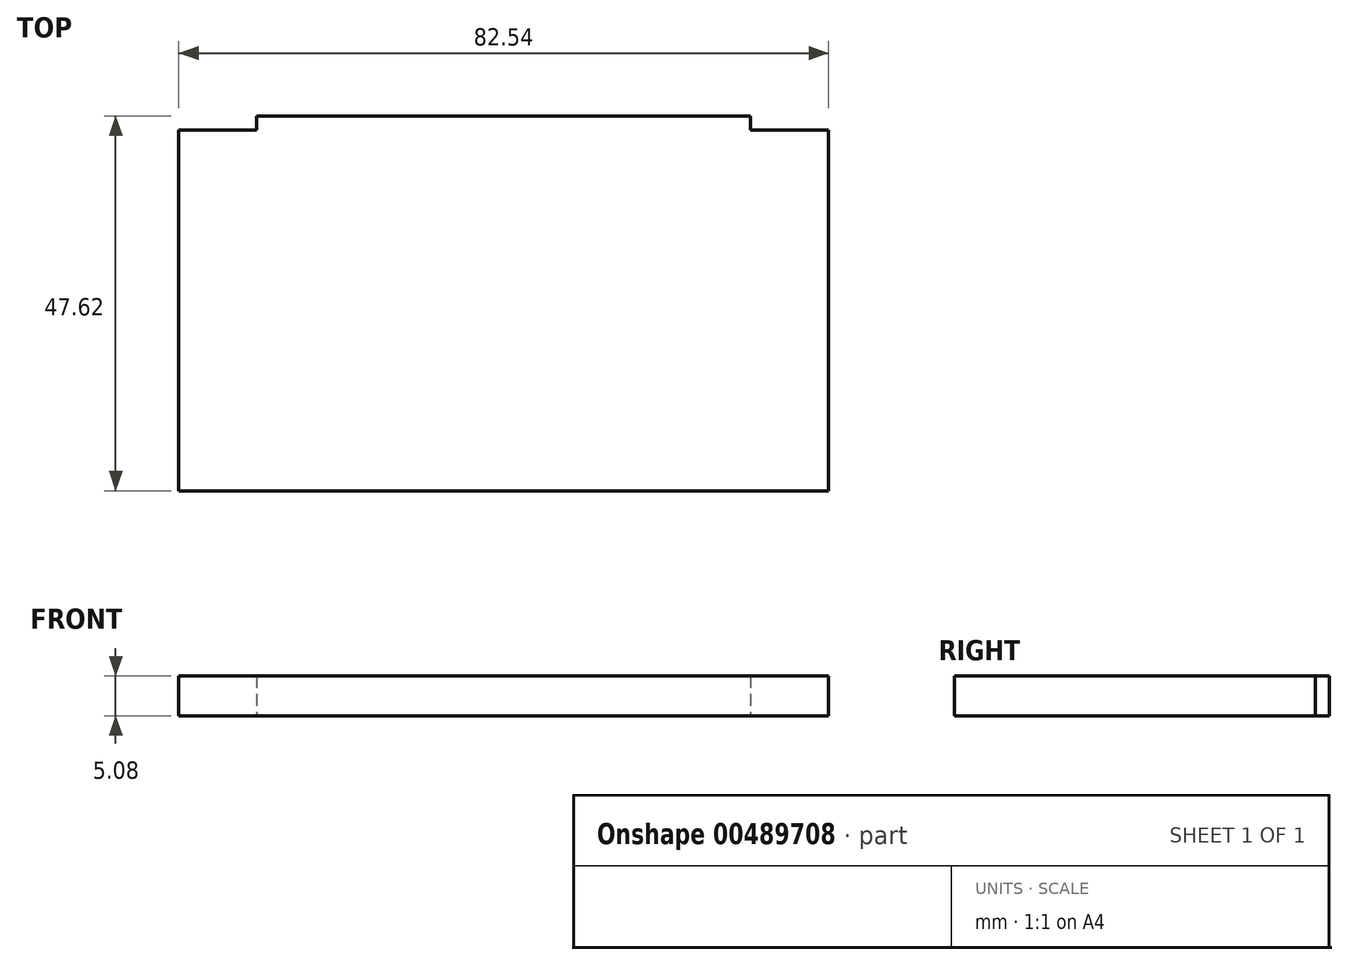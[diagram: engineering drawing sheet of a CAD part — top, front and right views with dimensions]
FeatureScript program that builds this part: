
annotation { "Feature Type Name" : "Feature", "Feature Type Description" : "" }
export const myFeature = defineFeature(function(context is Context, id is Id, definition is map)
    precondition{}
    {
        {
            var Q0;
            Q0=qCreatedBy(makeId("Top.planeOp"),FACE);
            var sketch = newSketch(context, id + "F0", { "sketchPlane" : qUnion([Q0])});
            skLineSegment(sketch, "E0.bottom", {"start": v(31.37, 23.81) * mm, "end": v(-31.37, 23.81) * mm});
            skLineSegment(sketch, "E0.top", {"start": v(41.28, -23.81) * mm, "end": v(-41.27, -23.81) * mm});
            skLineSegment(sketch, "E0.left", {"start": v(41.27, 22.03) * mm, "end": v(41.28, -23.81) * mm});
            skLineSegment(sketch, "E0.right", {"start": v(-41.28, 22.03) * mm, "end": v(-41.27, -23.81) * mm});
            skPoint(sketch, "E0.middle", {"position": v(0, 0) * mm});
            skLineSegment(sketch, "E1.top", {"start": v(-41.28, 22.03) * mm, "end": v(-31.37, 22.03) * mm});
            skLineSegment(sketch, "E1.right", {"start": v(-31.37, 23.81) * mm, "end": v(-31.37, 22.03) * mm});
            skLineSegment(sketch, "E2.MirrorCS", {"start": v(41.28, 22.03) * mm, "end": v(31.37, 22.03) * mm});
            skLineSegment(sketch, "E3.MirrorCS", {"start": v(31.37, 23.81) * mm, "end": v(31.37, 22.03) * mm});
            skPoint(sketch, "E4.orphan", {"position": v(41.27, 23.81) * mm});
            skPoint(sketch, "E5.orphan", {"position": v(-41.28, 23.81) * mm});
            skSolve(sketch);
        }
        {
            var Q0;
            Q0=makeQuery(id+"F0.imprint","IMPRINT",FACE,{"disambiguationData":[TD([[makeQuery(id+"F0.imprint","IMPRINT",EDGE,{"derivedFrom":sQuery(id+"F0.wireOp",EDGE,"E0.bottom")}),1.0]])]});
            extrude(context, id + "F1", {"entities" : qUnion([Q0]), "depth" : 5.08 * mm});
        }
    });
